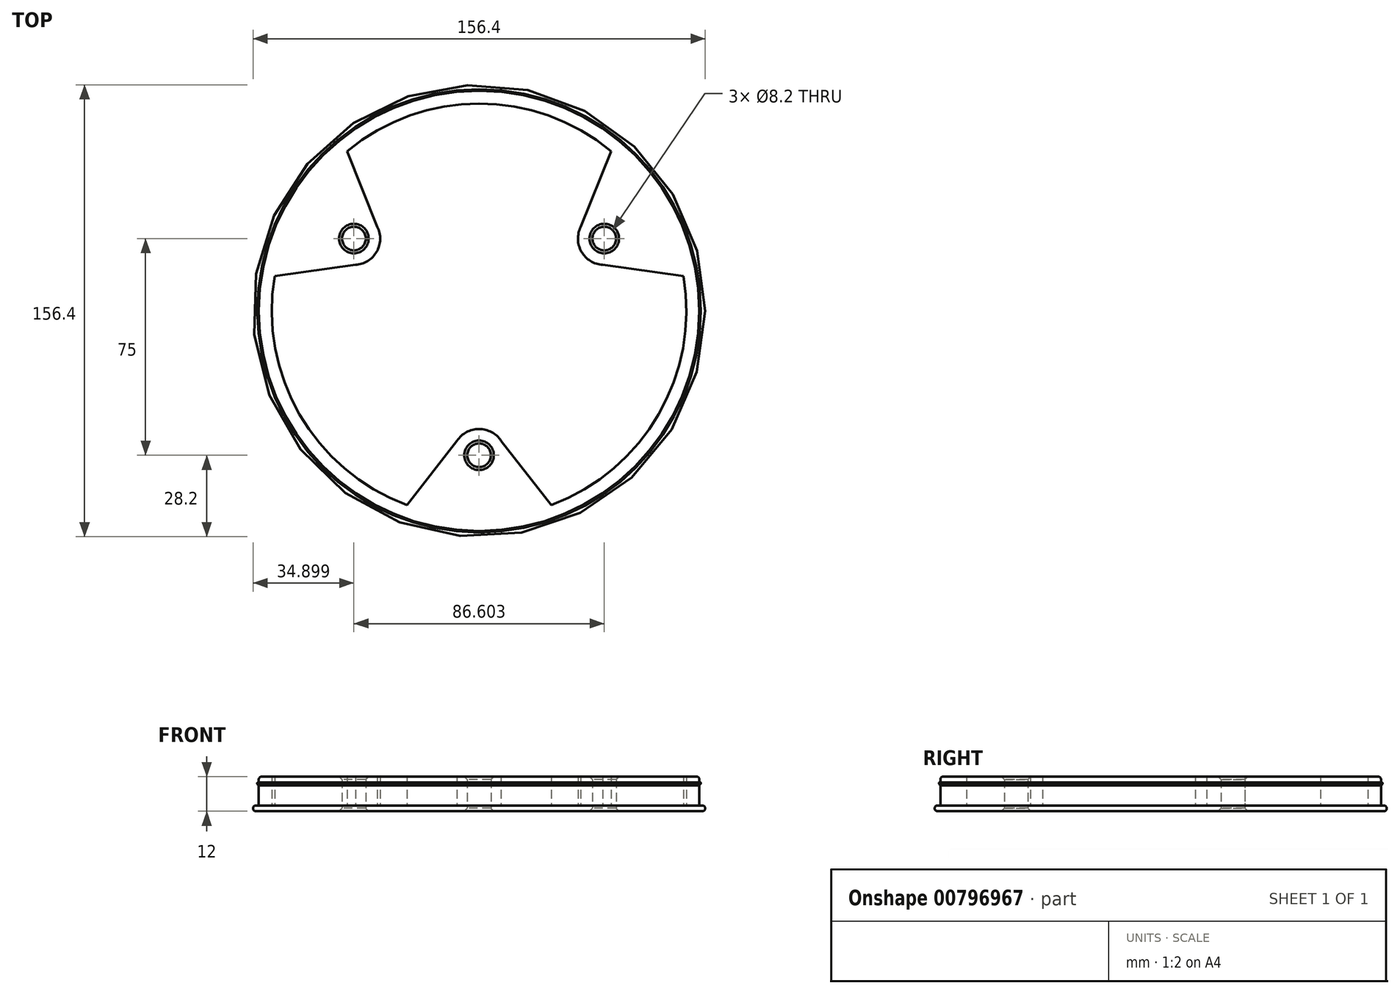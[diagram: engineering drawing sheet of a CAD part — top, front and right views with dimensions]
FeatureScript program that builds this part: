
annotation { "Feature Type Name" : "Feature", "Feature Type Description" : "" }
export const myFeature = defineFeature(function(context is Context, id is Id, definition is map)
    precondition{}
    {
        {
            assignVariable(context, id + "F0", {"name" : "LipH", "anyValue" : 2});
        }
        {
            var Q0;
            Q0=qCreatedBy(makeId("Top.planeOp"),FACE);
            var sketch = newSketch(context, id + "F1", { "sketchPlane" : qUnion([Q0])});
            skCircle(sketch, "E0", {"center": v(0, 0) * mm, "radius": 78.2 * mm});
            skSolve(sketch);
        }
        {
            var Q0;
            Q0 = qSketchRegion(id + "F1", true);
            extrude(context, id + "F2", {"entities" : qUnion([Q0]), "depth" : (getVariable(context, 'LipH')) * mm, "offsetDistance" : 25 * mm});
        }
        {
            assignVariable(context, id + "F3", {"name" : "WallH", "anyValue" : 10});
        }
        {
            var Q0;
            Q0=makeQuery(id+"F2.opExtrude","CAP_FACE",FACE,{"disambiguationData":[OSD([sQuery(id+"F1.wireOp",EDGE,"E0")])],"isStart":false});
            var sketch = newSketch(context, id + "F4", { "sketchPlane" : qUnion([Q0])});
            skCircle(sketch, "E1.0", {"center": v(0, 0) * mm, "radius": 76.2 * mm});
            skCircle(sketch, "E2.0", {"center": v(0, 0) * mm, "radius": 71.7 * mm});
            skSolve(sketch);
        }
        {
            var Q0;
            Q0 = qSketchRegion(id + "F4", true);
            extrude(context, id + "F5", {"entities" : qUnion([Q0]), "operationType" : NewBodyOperationType.ADD, "depth" : getVariable(context, 'WallH') * mm, "offsetDistance" : 25 * mm});
        }
        {
            var Q0;
            Q0=makeQuery(id+"F5.boolean.opBoolean","SPLIT",FACE,{"disambiguationData":[TD([makeQuery(id+"F5.opExtrude","SWEPT_FACE",FACE,{"disambiguationData":[OSD([sQuery(id+"F4.wireOp",EDGE,"E2.0")])]})])],"derivedFrom":makeQuery(id+"F2.opExtrude","CAP_FACE",FACE,{"disambiguationData":[OSD([sQuery(id+"F1.wireOp",EDGE,"E0")])],"isStart":false})});
            var sketch = newSketch(context, id + "F6", { "sketchPlane" : qUnion([Q0])});
            skCircle(sketch, "E3", {"center": v(0, -50) * mm, "radius": 4.1 * mm});
            skCircle(sketch, "E4.0", {"center": v(0, -50) * mm, "radius": 9.1 * mm});
            skLineSegment(sketch, "E5", {"start": v(-7.6, -45) * mm, "end": v(-25, -67.2) * mm});
            skLineSegment(sketch, "E6", {"start": v(7.6, -45) * mm, "end": v(25, -67.2) * mm});
            skCircle(sketch, "E7.1.0", {"center": v(-43.3, 25) * mm, "radius": 4.1 * mm});
            skCircle(sketch, "E7.1.1", {"center": v(-43.3, 25) * mm, "radius": 9.1 * mm});
            skLineSegment(sketch, "E7.1.2", {"start": v(-35.17, 29.08) * mm, "end": v(-45.7, 55.25) * mm});
            skLineSegment(sketch, "E7.1.3", {"start": v(-42.77, 15.92) * mm, "end": v(-70.7, 11.95) * mm});
            skCircle(sketch, "E7.2.0", {"center": v(43.3, 25) * mm, "radius": 4.1 * mm});
            skCircle(sketch, "E7.2.1", {"center": v(43.3, 25) * mm, "radius": 9.1 * mm});
            skLineSegment(sketch, "E7.2.2", {"start": v(42.77, 15.92) * mm, "end": v(70.7, 11.95) * mm});
            skLineSegment(sketch, "E7.2.3", {"start": v(35.17, 29.08) * mm, "end": v(45.7, 55.25) * mm});
            skPoint(sketch, "E7.center", {"position": v(0, 0) * mm});
            skLineSegment(sketch, "E7.anchor1", {"start": v(0, 0) * mm, "end": v(0, -50) * mm, "construction": true});
            skLineSegment(sketch, "E7.anchor2", {"start": v(0, 0) * mm, "end": v(43.3, 25) * mm, "construction": true});
            skSolve(sketch);
        }
        {
            var Q0;
            Q0 = qSketchRegion(id + "F6", true);
            var Q1;
            {var subQ0=sQuery(id+"F6.wireOp",EDGE,"E7.1.2");Q1=makeQuery(id+"F6.imprint","IMPRINT",FACE,{"disambiguationData":[TD([[makeQuery(id+"F6.imprint","IMPRINT",EDGE,{"derivedFrom":subQ0}),1.0]])]});}
            var Q2;
            {var subQ0=sQuery(id+"F6.wireOp",EDGE,"E7.2.2");Q2=makeQuery(id+"F6.imprint","IMPRINT",FACE,{"disambiguationData":[TD([[makeQuery(id+"F6.imprint","IMPRINT",EDGE,{"derivedFrom":subQ0}),1.0]])]});}
            var Q3;
            {var subQ0=sQuery(id+"F6.wireOp",EDGE,"E5");Q3=makeQuery(id+"F6.imprint","IMPRINT",FACE,{"disambiguationData":[TD([[makeQuery(id+"F6.imprint","IMPRINT",EDGE,{"derivedFrom":subQ0}),1.0]])]});}
            extrude(context, id + "F7", {"entities" : qUnion([Q0, Q1, Q2, Q3]), "operationType" : NewBodyOperationType.ADD, "depth" : getVariable(context, 'WallH') * mm, "offsetDistance" : 25 * mm});
        }
        {
            var Q0;
            {var subQ0=sQuery(id+"F4.wireOp",EDGE,"E2.0");Q0=makeQuery(id+"F7.boolean.opBoolean","MERGE",FACE,{"derivedFrom":[makeQuery(id+"F5.opExtrude","CAP_FACE",FACE,{"disambiguationData":[OSD([sQuery(id+"F4.wireOp",EDGE,"E1.0"),subQ0])],"isStart":false}),makeQuery(id+"F7.opExtrude","CAP_FACE",FACE,{"disambiguationData":[OSD([subQ0,sQuery(id+"F6.wireOp",EDGE,"E3"),sQuery(id+"F6.wireOp",EDGE,"E4.0"),sQuery(id+"F6.wireOp",EDGE,"E5"),sQuery(id+"F6.wireOp",EDGE,"E6")])],"isStart":false}),makeQuery(id+"F7.opExtrude","CAP_FACE",FACE,{"disambiguationData":[OSD([subQ0,sQuery(id+"F6.wireOp",EDGE,"E7.1.0"),sQuery(id+"F6.wireOp",EDGE,"E7.1.1"),sQuery(id+"F6.wireOp",EDGE,"E7.1.2"),sQuery(id+"F6.wireOp",EDGE,"E7.1.3")])],"isStart":false}),makeQuery(id+"F7.opExtrude","CAP_FACE",FACE,{"disambiguationData":[OSD([subQ0,sQuery(id+"F6.wireOp",EDGE,"E7.2.0"),sQuery(id+"F6.wireOp",EDGE,"E7.2.1"),sQuery(id+"F6.wireOp",EDGE,"E7.2.2"),sQuery(id+"F6.wireOp",EDGE,"E7.2.3")])],"isStart":false})]});}
            var sketch = newSketch(context, id + "F8", { "sketchPlane" : qUnion([Q0])});
            skCircle(sketch, "E8", {"center": v(0, -50) * mm, "radius": 4.1 * mm});
            skCircle(sketch, "E9", {"center": v(43.3, 25) * mm, "radius": 4.1 * mm});
            skCircle(sketch, "E10", {"center": v(-43.3, 25) * mm, "radius": 4.1 * mm});
            skSolve(sketch);
        }
        {
            var Q0;
            Q0 = qSketchRegion(id + "F8", true);
            extrude(context, id + "F9", {"entities" : qUnion([Q0]), "operationType" : NewBodyOperationType.REMOVE, "endBound" : BoundingType.THROUGH_ALL, "oppositeDirection" : true, "depth" : 25 * mm, "offsetDistance" : 25 * mm});
        }
        {
            var Q0;
            Q0=makeQuery(id+"F7.opExtrude","CAP_EDGE",EDGE,{"disambiguationData":[OSD([sQuery(id+"F6.wireOp",EDGE,"E7.1.0")])],"isStart":false});
            var Q1;
            Q1=makeQuery(id+"F7.opExtrude","CAP_EDGE",EDGE,{"disambiguationData":[OSD([sQuery(id+"F6.wireOp",EDGE,"E3")])],"isStart":false});
            var Q2;
            Q2=makeQuery(id+"F7.opExtrude","CAP_EDGE",EDGE,{"disambiguationData":[OSD([sQuery(id+"F6.wireOp",EDGE,"E7.2.0")])],"isStart":false});
            var Q3;
            Q3=makeQuery(id+"F9.boolean.opBoolean","INTERSECT",EDGE,{"derivedFrom":[makeQuery(id+"F2.opExtrude","CAP_FACE",FACE,{"disambiguationData":[OSD([sQuery(id+"F1.wireOp",EDGE,"E0")])],"isStart":true}),makeQuery(id+"F9.opExtrude","SWEPT_FACE",FACE,{"disambiguationData":[OSD([sQuery(id+"F8.wireOp",EDGE,"E8")])]})]});
            var Q4;
            Q4=makeQuery(id+"F9.boolean.opBoolean","INTERSECT",EDGE,{"derivedFrom":[makeQuery(id+"F2.opExtrude","CAP_FACE",FACE,{"disambiguationData":[OSD([sQuery(id+"F1.wireOp",EDGE,"E0")])],"isStart":true}),makeQuery(id+"F9.opExtrude","SWEPT_FACE",FACE,{"disambiguationData":[OSD([sQuery(id+"F8.wireOp",EDGE,"E9")])]})]});
            var Q5;
            Q5=makeQuery(id+"F9.boolean.opBoolean","INTERSECT",EDGE,{"derivedFrom":[makeQuery(id+"F2.opExtrude","CAP_FACE",FACE,{"disambiguationData":[OSD([sQuery(id+"F1.wireOp",EDGE,"E0")])],"isStart":true}),makeQuery(id+"F9.opExtrude","SWEPT_FACE",FACE,{"disambiguationData":[OSD([sQuery(id+"F8.wireOp",EDGE,"E10")])]})]});
            chamfer(context, id + "F10", {"entities" : qUnion([Q0, Q1, Q2, Q3, Q4, Q5]), "width" : 1 * mm, "tangentPropagation" : true});
        }
        {
            assignVariable(context, id + "F11", {"name" : "Flange", "anyValue" : .5});
        }
        {
            var Q0;
            {var subQ0=sQuery(id+"F1.wireOp",EDGE,"E0");Q0=makeQuery(id+"F5.boolean.opBoolean","SPLIT",FACE,{"disambiguationData":[TD([makeQuery(id+"F2.opExtrude","SWEPT_FACE",FACE,{"disambiguationData":[OSD([subQ0])]})])],"derivedFrom":makeQuery(id+"F2.opExtrude","CAP_FACE",FACE,{"disambiguationData":[OSD([subQ0])],"isStart":false})});}
            cPlane(context, id + "F12", {"entities" : qUnion([Q0]), "cplaneType" : CPlaneType.OFFSET, "offset" : 7.5 * mm, "width" : 150 * mm, "height" : 150 * mm});
        }
        {
            var Q0;
            Q0=qCreatedBy(id+"F12.planeOp",FACE);
            var sketch = newSketch(context, id + "F13", { "sketchPlane" : qUnion([Q0])});
            skCircle(sketch, "E11", {"center": v(0, 0) * mm, "radius": 76.2 * mm});
            skCircle(sketch, "E12.0", {"center": v(0, 0) * mm, "radius": 76.7 * mm});
            skSolve(sketch);
        }
        {
            var Q0;
            Q0 = qSketchRegion(id + "F13", true);
            extrude(context, id + "F14", {"entities" : qUnion([Q0]), "operationType" : NewBodyOperationType.ADD, "depth" : (getVariable(context, 'Flange')) * mm, "offsetDistance" : 25 * mm});
        }
        {
            var Q0;
            Q0=makeQuery(id+"F14.opExtrude","CAP_EDGE",EDGE,{"disambiguationData":[OSD([sQuery(id+"F13.wireOp",EDGE,"E12.0")])],"isStart":false});
            fillet(context, id + "F15", {"entities" : qUnion([Q0]), "radius" : .25 * mm, "tangentPropagation" : true, "allowEdgeOverflow" : false});
        }
        {
            var Q0;
            Q0=makeQuery(id+"F14.opExtrude","CAP_EDGE",EDGE,{"disambiguationData":[OSD([sQuery(id+"F13.wireOp",EDGE,"E11")])],"isStart":true});
            chamfer(context, id + "F16", {"entities" : qUnion([Q0]), "width" : .5 * mm, "tangentPropagation" : true});
        }
        {
            var Q0;
            Q0=makeQuery(id+"F2.opExtrude","CAP_EDGE",EDGE,{"disambiguationData":[OSD([sQuery(id+"F1.wireOp",EDGE,"E0")])],"isStart":false});
            var Q1;
            Q1=makeQuery(id+"F2.opExtrude","CAP_EDGE",EDGE,{"disambiguationData":[OSD([sQuery(id+"F1.wireOp",EDGE,"E0")])],"isStart":true});
            fillet(context, id + "F17", {"entities" : qUnion([Q0, Q1]), "radius" : 1 * mm, "tangentPropagation" : true, "allowEdgeOverflow" : false});
        }
        {
            var Q0;
            Q0=makeQuery(id+"F5.opExtrude","CAP_EDGE",EDGE,{"disambiguationData":[OSD([sQuery(id+"F4.wireOp",EDGE,"E1.0")])],"isStart":false});
            fillet(context, id + "F18", {"entities" : qUnion([Q0]), "radius" : 1 * mm, "tangentPropagation" : true, "allowEdgeOverflow" : false});
        }
    });
